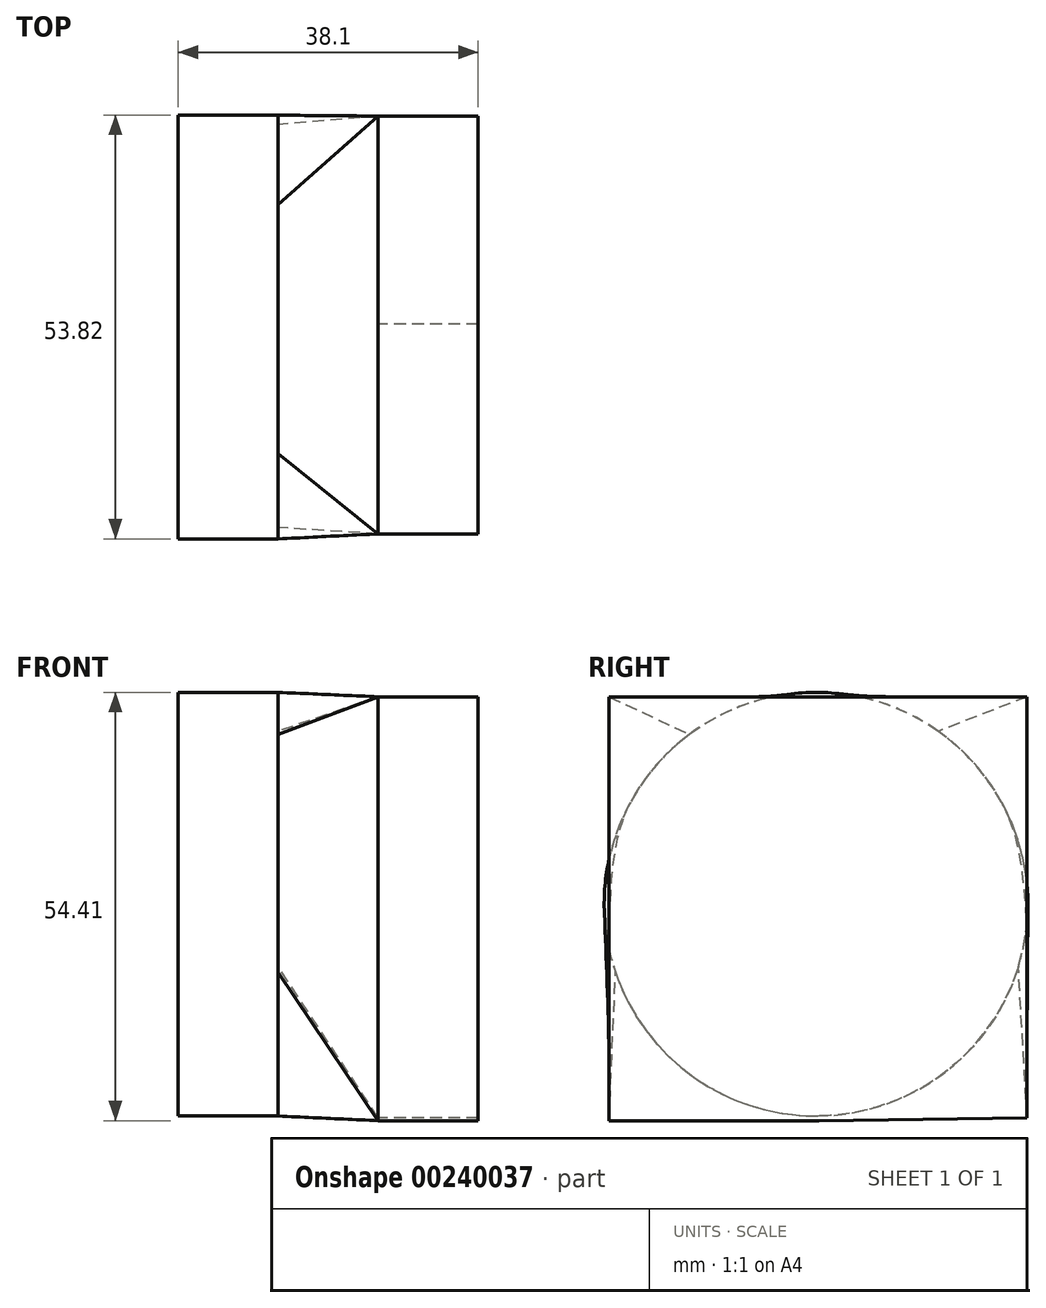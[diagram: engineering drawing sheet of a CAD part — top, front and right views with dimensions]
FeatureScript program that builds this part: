
annotation { "Feature Type Name" : "Feature", "Feature Type Description" : "" }
export const myFeature = defineFeature(function(context is Context, id is Id, definition is map)
    precondition{}
    {
        {
            var Q0;
            Q0=qCreatedBy(makeId("Right.planeOp"),FACE);
            cPlane(context, id + "F0", {"entities" : qUnion([Q0]), "cplaneType" : CPlaneType.OFFSET, "offset" : 25.4 * mm, "width" : 152.4 * mm, "height" : 152.4 * mm});
        }
        {
            var Q0;
            Q0=qCreatedBy(makeId("Right.planeOp"),FACE);
            var sketch = newSketch(context, id + "F1", { "sketchPlane" : qUnion([Q0])});
            skCircle(sketch, "E0", {"center": v(-41.23, 31.43) * mm, "radius": 26.91 * mm});
            skSolve(sketch);
        }
        {
            var Q0;
            Q0=makeQuery(id+"F1.imprint","IMPRINT",FACE,{"disambiguationData":[TD([[makeQuery(id+"F1.imprint","IMPRINT",EDGE,{"derivedFrom":sQuery(id+"F1.wireOp",EDGE,"E0")}),1.0]])]});
            extrude(context, id + "F2", {"entities" : qUnion([Q0]), "depth" : 12.7 * mm});
        }
        {
            var Q0;
            Q0=qCreatedBy(id+"F0.planeOp",FACE);
            var sketch = newSketch(context, id + "F3", { "sketchPlane" : qUnion([Q0])});
            skLineSegment(sketch, "E1", {"start": v(-40.87, 3.93) * mm, "end": v(-67.5, 3.93) * mm});
            skLineSegment(sketch, "E2", {"start": v(-67.5, 3.93) * mm, "end": v(-67.5, 57.78) * mm});
            skLineSegment(sketch, "E3", {"start": v(-67.5, 57.78) * mm, "end": v(-14.43, 57.78) * mm});
            skLineSegment(sketch, "E4", {"start": v(-14.43, 57.78) * mm, "end": v(-14.43, 4.32) * mm});
            skLineSegment(sketch, "E5", {"start": v(-14.43, 4.32) * mm, "end": v(-40.87, 3.93) * mm});
            skSolve(sketch);
        }
        {
            var Q0;
            Q0=makeQuery(id+"F3.imprint","IMPRINT",FACE,{"disambiguationData":[TD([[makeQuery(id+"F3.imprint","IMPRINT",EDGE,{"derivedFrom":sQuery(id+"F3.wireOp",EDGE,"E1")}),-1.0]])]});
            extrude(context, id + "F4", {"entities" : qUnion([Q0]), "depth" : 12.7 * mm});
        }
        {
            var Q1;
            Q1=makeQuery(id+"F4.opExtrude","CAP_FACE",FACE,{"disambiguationData":[OSD([sQuery(id+"F3.wireOp",EDGE,"E1"),sQuery(id+"F3.wireOp",EDGE,"E2"),sQuery(id+"F3.wireOp",EDGE,"E3"),sQuery(id+"F3.wireOp",EDGE,"E4"),sQuery(id+"F3.wireOp",EDGE,"E5")])],"isStart":true});
            var Q2;
            Q2=makeQuery(id+"F2.opExtrude","CAP_FACE",FACE,{"disambiguationData":[OSD([sQuery(id+"F1.wireOp",EDGE,"E0")])],"isStart":false});
            loft(context, id + "F5", {"operationType" : NewBodyOperationType.ADD, "sheetProfilesArray" : [{ "sheetProfileEntities" : qUnion([Q1]) }, { "sheetProfileEntities" : qUnion([Q2]) }]});
        }
    });
